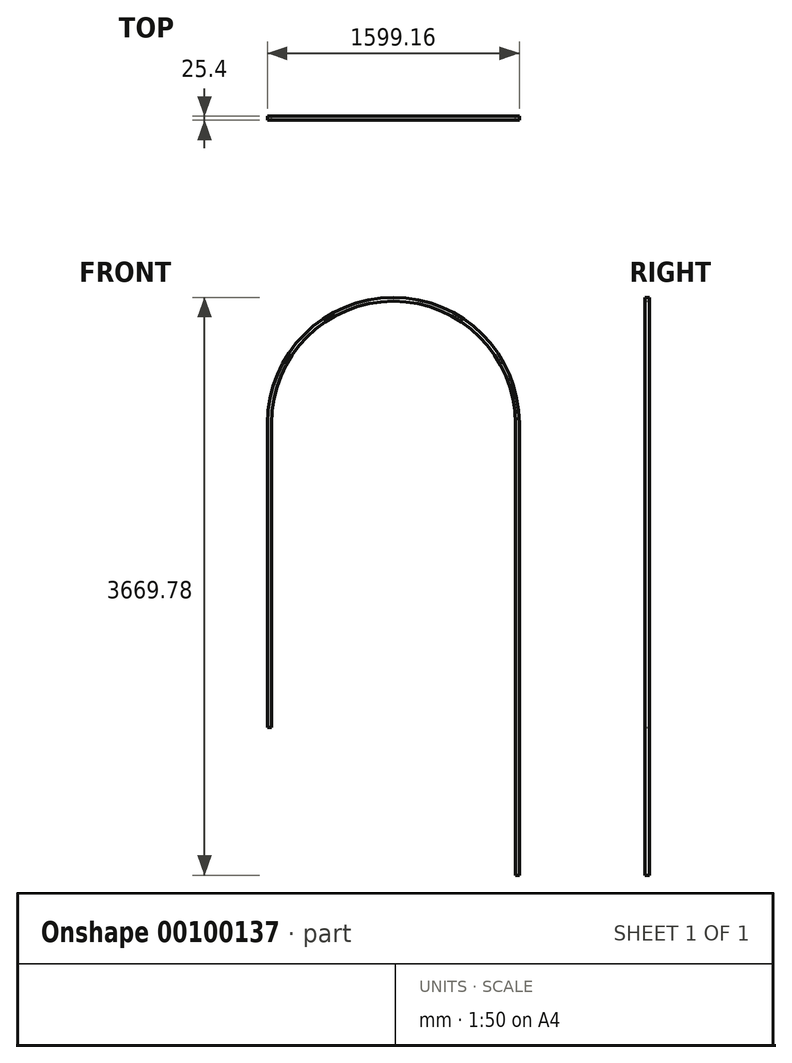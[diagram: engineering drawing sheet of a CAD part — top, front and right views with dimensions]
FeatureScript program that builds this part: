
annotation { "Feature Type Name" : "Feature", "Feature Type Description" : "" }
export const myFeature = defineFeature(function(context is Context, id is Id, definition is map)
    precondition{}
    {
        {
            var Q0;
            Q0=qCreatedBy(makeId("Front.planeOp"),FACE);
            var sketch = newSketch(context, id + "F0", { "sketchPlane" : qUnion([Q0])});
            skLineSegment(sketch, "E0", {"start": v(0, 0) * mm, "end": v(0, 1930.4) * mm});
            skArc(sketch, "E1", {"start": v(0, 1930.4) * mm, "mid": v(787.4, 2717.8) * mm, "end": v(1574.8, 1930.4) * mm});
            skLineSegment(sketch, "E2", {"start": v(1574.8, 1930.4) * mm, "end": v(1574.8, -939.8) * mm});
            skSolve(sketch);
        }
        {
            var Q0;
            Q0=qCreatedBy(makeId("Top.planeOp"),FACE);
            var sketch = newSketch(context, id + "F1", { "sketchPlane" : qUnion([Q0])});
            skLineSegment(sketch, "E3.bottom", {"start": v(12.18, -12.7) * mm, "end": v(-12.18, -12.7) * mm});
            skLineSegment(sketch, "E3.top", {"start": v(12.18, 12.7) * mm, "end": v(-12.18, 12.7) * mm});
            skLineSegment(sketch, "E3.left", {"start": v(12.18, -12.7) * mm, "end": v(12.18, 12.7) * mm});
            skLineSegment(sketch, "E3.right", {"start": v(-12.18, -12.7) * mm, "end": v(-12.18, 12.7) * mm});
            skPoint(sketch, "E3.middle", {"position": v(0, 0) * mm});
            skSolve(sketch);
        }
        {
            var Q0;
            Q0 = qSketchRegion(id + "F1", true);
            var Q1;
            Q1 = qConstructionFilter(qBodyType(qCreatedBy(id + "F0" ,EDGE), BodyType.WIRE), ConstructionObject.NO);
            sweep(context, id + "F2", {"profiles" : qUnion([Q0]), "path" : qUnion([Q1])});
        }
    });
